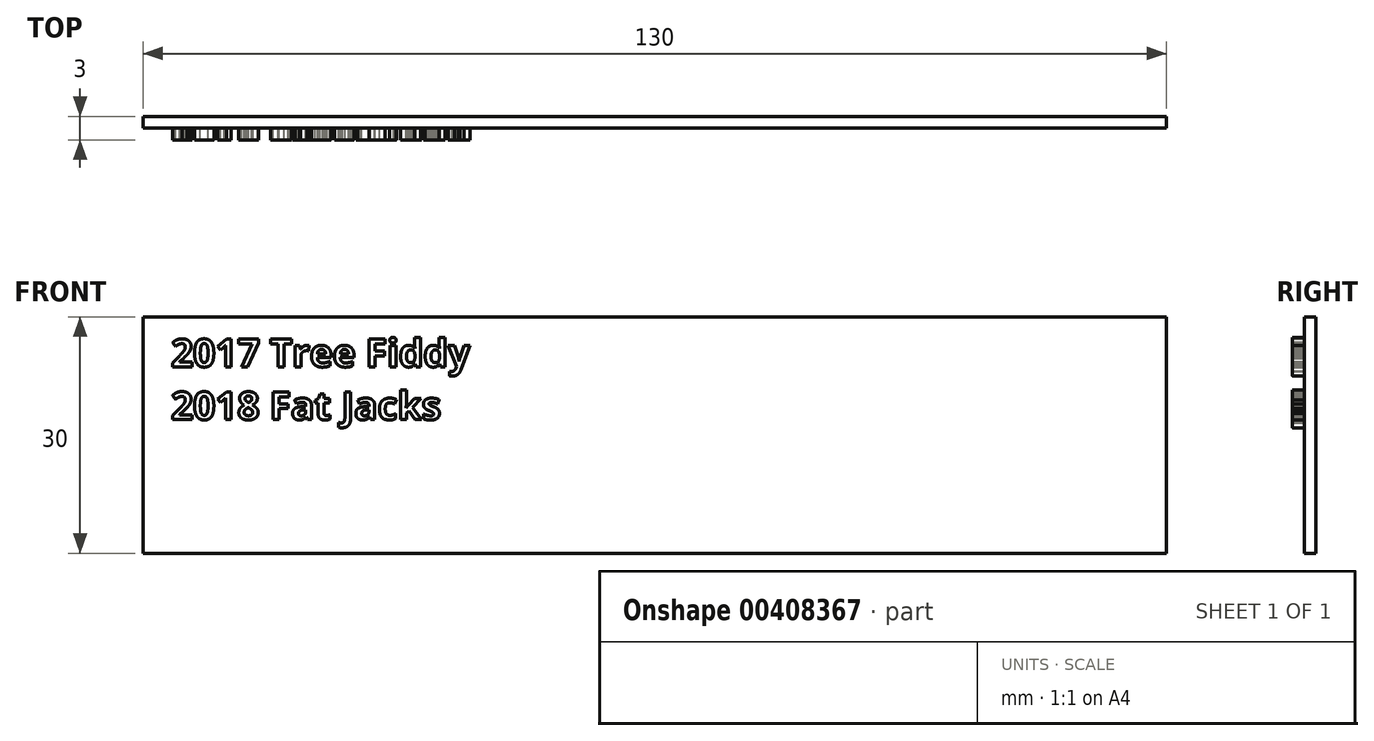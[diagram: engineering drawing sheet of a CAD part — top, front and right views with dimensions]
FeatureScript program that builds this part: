
annotation { "Feature Type Name" : "Feature", "Feature Type Description" : "" }
export const myFeature = defineFeature(function(context is Context, id is Id, definition is map)
    precondition{}
    {
        {
            var Q0;
            Q0=qCreatedBy(makeId("Front.planeOp"),FACE);
            var sketch = newSketch(context, id + "F0", { "sketchPlane" : qUnion([Q0])});
            skLineSegment(sketch, "E0", {"start": v(0, 0) * mm, "end": v(65, 0) * mm});
            skLineSegment(sketch, "E1", {"start": v(65, 0) * mm, "end": v(65, 30) * mm});
            skLineSegment(sketch, "E2", {"start": v(65, 30) * mm, "end": v(0, 30) * mm});
            skLineSegment(sketch, "E3", {"start": v(0, 30) * mm, "end": v(0, 0) * mm});
            skLineSegment(sketch, "E4.MirrorCS", {"start": v(-65, 30) * mm, "end": v(0, 30) * mm});
            skLineSegment(sketch, "E5.MirrorCS", {"start": v(-65, 0) * mm, "end": v(-65, 30) * mm});
            skLineSegment(sketch, "E6.MirrorCS", {"start": v(0, 0) * mm, "end": v(-65, 0) * mm});
            skSolve(sketch);
        }
        {
            var Q0;
            Q0=makeQuery(id+"F0.imprint","IMPRINT",FACE,{"disambiguationData":[TD([[makeQuery(id+"F0.imprint","IMPRINT",EDGE,{"derivedFrom":sQuery(id+"F0.wireOp",EDGE,"E0")}),1.0]])]});
            var Q1;
            Q1=makeQuery(id+"F0.imprint","IMPRINT",FACE,{"disambiguationData":[TD([[makeQuery(id+"F0.imprint","IMPRINT",EDGE,{"derivedFrom":sQuery(id+"F0.wireOp",EDGE,"E3")}),-1.0]])]});
            extrude(context, id + "F1", {"entities" : qUnion([Q0, Q1]), "depth" : 1.5 * mm});
        }
        {
            var Q0;
            {var subQ0=sQuery(id+"F0.wireOp",EDGE,"E6.MirrorCS");var subQ1=sQuery(id+"F0.wireOp",EDGE,"E0");var subQ2=sQuery(id+"F0.wireOp",EDGE,"E1");var subQ3=sQuery(id+"F0.wireOp",EDGE,"E5.MirrorCS");var subQ4=sQuery(id+"F0.wireOp",EDGE,"E4.MirrorCS");var subQ5=sQuery(id+"F0.wireOp",EDGE,"E2");Q0=makeQuery(id+"Fk1N3MaAwcA2FfH_1.boolean.opBoolean","SPLIT",FACE,{"disambiguationData":[TD([makeQuery(id+"F1.opExtrude","SWEPT_FACE",FACE,{"disambiguationData":[OSD([subQ2])]})])],"derivedFrom":makeQuery(id+"F1.opExtrude","CAP_FACE",FACE,{"disambiguationData":[OSD([subQ1,subQ2,subQ5,subQ4,subQ3,subQ0])],"isStart":false})});}
            var sketch = newSketch(context, id + "F2", { "sketchPlane" : qUnion([Q0])});
            skText(sketch, "E7", { "text": "2017 Tree Fiddy\n2018 Fat Jacks", "fontName": "OpenSans-Bold.ttf"});
            const initialGuessF2  = {"E7": [-0.06146, 0.02367, 1, 0, 0.00355]};
            skSetInitialGuess(sketch, initialGuessF2);
            skSolve(sketch);
        }
        {
            var Q0;
            Q0=qSketchRegion(id+"F2",true);
            extrude(context, id + "F3", {"entities" : qUnion([Q0]), "operationType" : NewBodyOperationType.ADD, "depth" : 1.5 * mm});
        }
    });
